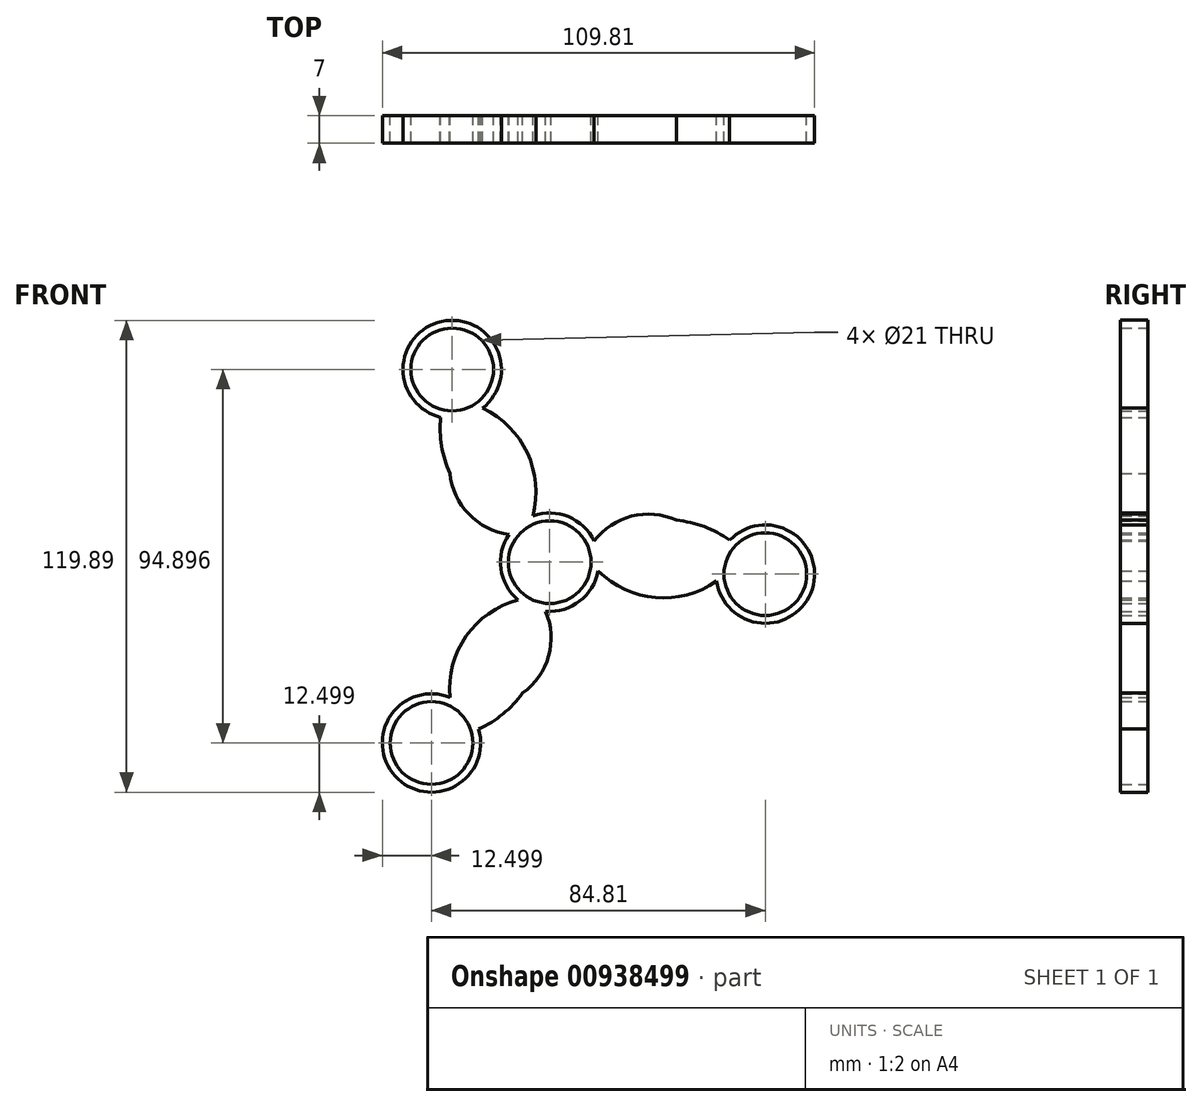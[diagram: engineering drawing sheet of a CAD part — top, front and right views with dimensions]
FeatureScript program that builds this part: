
annotation { "Feature Type Name" : "Feature", "Feature Type Description" : "" }
export const myFeature = defineFeature(function(context is Context, id is Id, definition is map)
    precondition{}
    {
        {
            var Q0;
            Q0=qCreatedBy(makeId("Front.planeOp"),FACE);
            var sketch = newSketch(context, id + "F0", { "sketchPlane" : qUnion([Q0])});
            skCircle(sketch, "E0", {"center": v(0, 0) * mm, "radius": 10.5 * mm});
            skCircle(sketch, "E1.0", {"center": v(0, 0) * mm, "radius": 12.5 * mm});
            skArc(sketch, "E2", {"start": v(-25.35, 22.57) * mm, "mid": v(-20.53, 12.2) * mm, "end": v(-10.28, 7.1) * mm});
            skArc(sketch, "E3", {"start": v(-4.28, 11.75) * mm, "mid": v(-5.68, 27.76) * mm, "end": v(-17.04, 39.14) * mm});
            skCircle(sketch, "E4", {"center": v(-24.77, 48.96) * mm, "radius": 10.5 * mm});
            skCircle(sketch, "E5.0", {"center": v(-24.77, 48.96) * mm, "radius": 12.5 * mm});
            skArc(sketch, "E6", {"start": v(-27.7, 36.81) * mm, "mid": v(-27.46, 29.54) * mm, "end": v(-25.35, 22.57) * mm});
            skPoint(sketch, "E7", {"position": v(-25.35, 22.57) * mm});
            skArc(sketch, "E8.1.0", {"start": v(-8.03, -9.58) * mm, "mid": v(-21.2, -18.8) * mm, "end": v(-25.37, -34.33) * mm});
            skArc(sketch, "E8.1.1", {"start": v(-6.87, -33.24) * mm, "mid": v(-0.3, -23.88) * mm, "end": v(-1.01, -12.46) * mm});
            skArc(sketch, "E8.1.2", {"start": v(-18.03, -42.4) * mm, "mid": v(-11.85, -38.55) * mm, "end": v(-6.87, -33.24) * mm});
            skCircle(sketch, "E8.1.3", {"center": v(-30.02, -45.93) * mm, "radius": 10.5 * mm});
            skCircle(sketch, "E8.1.4", {"center": v(-30.02, -45.93) * mm, "radius": 12.5 * mm});
            skArc(sketch, "E8.2.0", {"start": v(12.31, -2.17) * mm, "mid": v(26.88, -8.96) * mm, "end": v(42.42, -4.81) * mm});
            skArc(sketch, "E8.2.1", {"start": v(32.22, 10.67) * mm, "mid": v(20.82, 11.68) * mm, "end": v(11.3, 5.35) * mm});
            skArc(sketch, "E8.2.2", {"start": v(45.73, 5.58) * mm, "mid": v(39.3, 9.01) * mm, "end": v(32.22, 10.67) * mm});
            skCircle(sketch, "E8.2.3", {"center": v(54.79, -3.03) * mm, "radius": 10.5 * mm});
            skCircle(sketch, "E8.2.4", {"center": v(54.79, -3.03) * mm, "radius": 12.5 * mm});
            skCircle(sketch, "E9", {"center": v(37.73, -42.4) * mm, "radius": 10.5 * mm});
            skCircle(sketch, "E10", {"center": v(37.73, -42.4) * mm, "radius": 4.25 * mm});
            skCircle(sketch, "E11", {"center": v(37.73, -42.4) * mm, "radius": 3.25 * mm});
            skSolve(sketch);
        }
        {
            var Q0;
            {var subQ1=sQuery(id+"F0.wireOp",EDGE,"E8.2.0");Q0=makeQuery(id+"F0.imprint","IMPRINT",FACE,{"disambiguationData":[TD([[makeQuery(id+"F0.imprint","IMPRINT",EDGE,{"derivedFrom":subQ1}),1.0]])]});}
            var Q1;
            Q1=makeQuery(id+"F0.imprint","IMPRINT",FACE,{"disambiguationData":[TD([[makeQuery(id+"F0.imprint","IMPRINT",EDGE,{"derivedFrom":sQuery(id+"F0.wireOp",EDGE,"E8.2.3")}),-1.0]])]});
            var Q2;
            Q2=makeQuery(id+"F0.imprint","IMPRINT",FACE,{"disambiguationData":[TD([[makeQuery(id+"F0.imprint","IMPRINT",EDGE,{"derivedFrom":sQuery(id+"F0.wireOp",EDGE,"E4")}),-1.0]])]});
            var Q3;
            {var subQ3=sQuery(id+"F0.wireOp",EDGE,"E2");Q3=makeQuery(id+"F0.imprint","IMPRINT",FACE,{"disambiguationData":[TD([[makeQuery(id+"F0.imprint","IMPRINT",EDGE,{"derivedFrom":subQ3}),1.0]])]});}
            var Q4;
            Q4=makeQuery(id+"F0.imprint","IMPRINT",FACE,{"disambiguationData":[TD([[makeQuery(id+"F0.imprint","IMPRINT",EDGE,{"derivedFrom":sQuery(id+"F0.wireOp",EDGE,"E0")}),-1.0]])]});
            var Q5;
            {var subQ1=sQuery(id+"F0.wireOp",EDGE,"E8.1.0");Q5=makeQuery(id+"F0.imprint","IMPRINT",FACE,{"disambiguationData":[TD([[makeQuery(id+"F0.imprint","IMPRINT",EDGE,{"derivedFrom":subQ1}),1.0]])]});}
            var Q6;
            Q6=makeQuery(id+"F0.imprint","IMPRINT",FACE,{"disambiguationData":[TD([[makeQuery(id+"F0.imprint","IMPRINT",EDGE,{"derivedFrom":sQuery(id+"F0.wireOp",EDGE,"E8.1.3")}),-1.0]])]});
            extrude(context, id + "F1", {"entities" : qUnion([Q0, Q1, Q2, Q3, Q4, Q5, Q6]), "depth" : 7 * mm, "offsetDistance" : 25 * mm});
        }
    });
